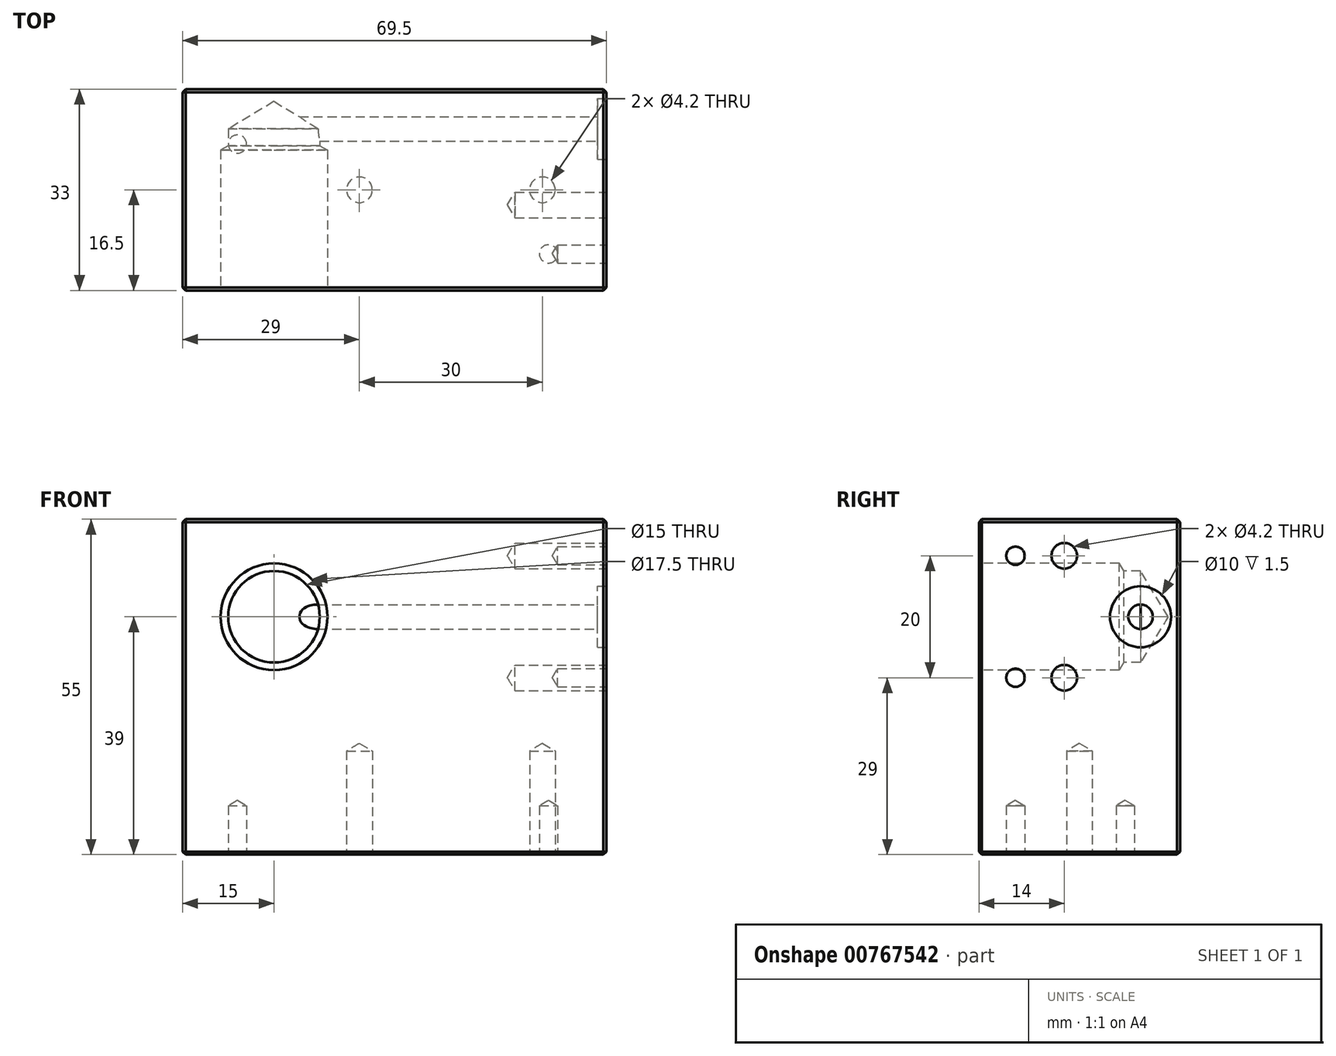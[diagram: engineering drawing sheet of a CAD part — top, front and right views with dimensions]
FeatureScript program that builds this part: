
annotation { "Feature Type Name" : "Feature", "Feature Type Description" : "" }
export const myFeature = defineFeature(function(context is Context, id is Id, definition is map)
    precondition{}
    {
        {
            var Q0;
            Q0=qCreatedBy(makeId("Front.planeOp"),FACE);
            var sketch = newSketch(context, id + "F0", { "sketchPlane" : qUnion([Q0])});
            skLineSegment(sketch, "E0.bottom", {"start": v(0, 0) * mm, "end": v(69.5, 0) * mm});
            skLineSegment(sketch, "E0.top", {"start": v(0, 55) * mm, "end": v(69.5, 55) * mm});
            skLineSegment(sketch, "E0.left", {"start": v(0, 0) * mm, "end": v(0, 55) * mm});
            skLineSegment(sketch, "E0.right", {"start": v(69.5, 0) * mm, "end": v(69.5, 55) * mm});
            skSolve(sketch);
        }
        {
            var Q0;
            Q0 = qSketchRegion(id + "F0", true);
            extrude(context, id + "F1", {"entities" : qUnion([Q0]), "oppositeDirection" : true, "depth" : 33 * mm, "offsetDistance" : 25 * mm});
        }
        {
            var Q0;
            Q0=makeQuery(id+"F1.opExtrude","CAP_FACE",FACE,{"disambiguationData":[OSD([sQuery(id+"F0.wireOp",EDGE,"E0.bottom"),sQuery(id+"F0.wireOp",EDGE,"E0.top"),sQuery(id+"F0.wireOp",EDGE,"E0.left"),sQuery(id+"F0.wireOp",EDGE,"E0.right")])],"isStart":true});
            var Q1;
            Q1=makeQuery(id+"F1.opExtrude","CAP_FACE",FACE,{"disambiguationData":[OSD([sQuery(id+"F0.wireOp",EDGE,"E0.bottom"),sQuery(id+"F0.wireOp",EDGE,"E0.top"),sQuery(id+"F0.wireOp",EDGE,"E0.left"),sQuery(id+"F0.wireOp",EDGE,"E0.right")])],"isStart":false});
            var Q2;
            Q2=makeQuery(id+"F1.opExtrude","SWEPT_FACE",FACE,{"disambiguationData":[OSD([sQuery(id+"F0.wireOp",EDGE,"E0.top")])]});
            var Q3;
            Q3=makeQuery(id+"F1.opExtrude","SWEPT_FACE",FACE,{"disambiguationData":[OSD([sQuery(id+"F0.wireOp",EDGE,"E0.left")])]});
            var Q4;
            Q4=makeQuery(id+"F1.opExtrude","SWEPT_FACE",FACE,{"disambiguationData":[OSD([sQuery(id+"F0.wireOp",EDGE,"E0.right")])]});
            var Q5;
            Q5=makeQuery(id+"F1.opExtrude","SWEPT_FACE",FACE,{"disambiguationData":[OSD([sQuery(id+"F0.wireOp",EDGE,"E0.bottom")])]});
            chamfer(context, id + "F2", {"entities" : qUnion([Q0, Q1, Q2, Q3, Q4, Q5]), "width" : 0.5 * mm, "tangentPropagation" : true});
        }
        {
            var Q0;
            Q0=qCreatedBy(makeId("Front.planeOp"),FACE);
            var sketch = newSketch(context, id + "F3", { "sketchPlane" : qUnion([Q0])});
            skPoint(sketch, "E1", {"position": v(15, 39) * mm});
            skSolve(sketch);
        }
        {
            var Q0;
            Q0=sQuery(id+"F3.wireOp",VERTEX,"E1");
            var Q1;
            Q1=makeQuery(id+"F1.opExtrude","SWEPT_BODY",BODY,{"disambiguationData":[OSD([sQuery(id+"F0.wireOp",EDGE,"E0.bottom"),sQuery(id+"F0.wireOp",EDGE,"E0.top"),sQuery(id+"F0.wireOp",EDGE,"E0.left"),sQuery(id+"F0.wireOp",EDGE,"E0.right")])]});
            hole(context, id + "F4", {"style" : HoleStyle.SIMPLE, "endStyle" : HoleEndStyle.BLIND, "standardTappedOrClearance" : lookupTablePath({ "standard" : "ISO", "engagement" : "75%", "pitch" : "2.5 mm", "size" : "M20", "type" : "Tapped" }), "standardBlindInLast" : lookupTablePath({ "standard" : "ISO", "engagement" : "75%", "pitch" : "2.5 mm", "size" : "M20", "type" : "Tapped" }), "holeDiameter" : 17.5 * mm, "majorDiameter" : 20 * mm, "showTappedDepth" : true, "holeDepth" : 23 * mm, "tappedDepth" : 18 * mm, "tapClearance" : 2, "startFromSketch" : true, "locations" : qUnion([Q0]), "scope" : qUnion([Q1])});
        }
        {
            var Q0;
            Q0=sQuery(id+"F3.wireOp",VERTEX,"E1");
            var Q1;
            Q1=makeQuery(id+"F1.opExtrude","SWEPT_BODY",BODY,{"disambiguationData":[OSD([sQuery(id+"F0.wireOp",EDGE,"E0.bottom"),sQuery(id+"F0.wireOp",EDGE,"E0.top"),sQuery(id+"F0.wireOp",EDGE,"E0.left"),sQuery(id+"F0.wireOp",EDGE,"E0.right")])]});
            hole(context, id + "F5", {"style" : HoleStyle.SIMPLE, "endStyle" : HoleEndStyle.BLIND, "holeDiameter" : 15 * mm, "majorDiameter" : 20 * mm, "holeDepth" : 26.5 * mm, "tappedDepth" : 18 * mm, "tapClearance" : 2, "startFromSketch" : true, "locations" : qUnion([Q0]), "scope" : qUnion([Q1])});
        }
        {
            var Q0;
            Q0=makeQuery(id+"F1.opExtrude","SWEPT_FACE",FACE,{"disambiguationData":[OSD([sQuery(id+"F0.wireOp",EDGE,"E0.right")])]});
            var sketch = newSketch(context, id + "F6", { "sketchPlane" : qUnion([Q0])});
            skPoint(sketch, "E2", {"position": v(26.5, 39) * mm});
            skPoint(sketch, "E3", {"position": v(14, 49) * mm});
            skPoint(sketch, "E4", {"position": v(14, 29) * mm});
            skPoint(sketch, "E5", {"position": v(6, 49) * mm});
            skPoint(sketch, "E6", {"position": v(6, 29) * mm});
            skLineSegment(sketch, "E7", {"start": v(6, 49) * mm, "end": v(6, 29) * mm, "construction": true});
            skLineSegment(sketch, "E8", {"start": v(14, 49) * mm, "end": v(14, 29) * mm, "construction": true});
            skLineSegment(sketch, "E9", {"start": v(6, 49) * mm, "end": v(14, 49) * mm, "construction": true});
            skLineSegment(sketch, "E10", {"start": v(6, 29) * mm, "end": v(14, 29) * mm, "construction": true});
            skSolve(sketch);
        }
        {
            var Q0;
            Q0=qCreatedBy(makeId("Top.planeOp"),FACE);
            var sketch = newSketch(context, id + "F7", { "sketchPlane" : qUnion([Q0])});
            skPoint(sketch, "E11", {"position": v(9, 24) * mm});
            skPoint(sketch, "E12", {"position": v(60, 6) * mm});
            skPoint(sketch, "E13", {"position": v(59, 16.5) * mm});
            skPoint(sketch, "E14", {"position": v(29, 16.5) * mm});
            skLineSegment(sketch, "E15", {"start": v(29, 16.5) * mm, "end": v(59, 16.5) * mm, "construction": true});
            skSolve(sketch);
        }
        {
            var Q0;
            Q0=sQuery(id+"F6.wireOp",VERTEX,"E2");
            var Q1;
            Q1=makeQuery(id+"F1.opExtrude","SWEPT_BODY",BODY,{"disambiguationData":[OSD([sQuery(id+"F0.wireOp",EDGE,"E0.bottom"),sQuery(id+"F0.wireOp",EDGE,"E0.top"),sQuery(id+"F0.wireOp",EDGE,"E0.left"),sQuery(id+"F0.wireOp",EDGE,"E0.right")])]});
            hole(context, id + "F8", {"style" : HoleStyle.C_BORE, "endStyle" : HoleEndStyle.BLIND, "holeDiameter" : 4 * mm, "cBoreDiameter" : 10 * mm, "cBoreDepth" : 1.5 * mm, "majorDiameter" : 5 * mm, "holeDepth" : (69.5 - 15) * mm, "tappedDepth" : 18 * mm, "tapClearance" : 2, "startFromSketch" : true, "locations" : qUnion([Q0]), "scope" : qUnion([Q1])});
        }
        {
            var Q0;
            Q0=sQuery(id+"F6.wireOp",VERTEX,"E3");
            var Q1;
            Q1=sQuery(id+"F6.wireOp",VERTEX,"E4");
            var Q2;
            Q2=makeQuery(id+"F1.opExtrude","SWEPT_BODY",BODY,{"disambiguationData":[OSD([sQuery(id+"F0.wireOp",EDGE,"E0.bottom"),sQuery(id+"F0.wireOp",EDGE,"E0.top"),sQuery(id+"F0.wireOp",EDGE,"E0.left"),sQuery(id+"F0.wireOp",EDGE,"E0.right")])]});
            hole(context, id + "F9", {"style" : HoleStyle.SIMPLE, "endStyle" : HoleEndStyle.BLIND, "standardTappedOrClearance" : lookupTablePath({ "standard" : "ISO", "engagement" : "75%", "pitch" : "0.8 mm", "size" : "M5", "type" : "Tapped" }), "standardBlindInLast" : lookupTablePath({ "standard" : "ISO", "engagement" : "75%", "pitch" : "0.8 mm", "size" : "M5", "type" : "Tapped" }), "holeDiameter" : 4.2 * mm, "majorDiameter" : 5 * mm, "showTappedDepth" : true, "holeDepth" : 15 * mm, "tappedDepth" : 11.8 * mm, "tapClearance" : 4, "startFromSketch" : true, "locations" : qUnion([Q0, Q1]), "scope" : qUnion([Q2])});
        }
        {
            var Q0;
            Q0=sQuery(id+"F6.wireOp",VERTEX,"E5");
            var Q1;
            Q1=sQuery(id+"F6.wireOp",VERTEX,"E6");
            var Q2;
            Q2=makeQuery(id+"F1.opExtrude","SWEPT_BODY",BODY,{"disambiguationData":[OSD([sQuery(id+"F0.wireOp",EDGE,"E0.bottom"),sQuery(id+"F0.wireOp",EDGE,"E0.top"),sQuery(id+"F0.wireOp",EDGE,"E0.left"),sQuery(id+"F0.wireOp",EDGE,"E0.right")])]});
            hole(context, id + "F10", {"style" : HoleStyle.SIMPLE, "endStyle" : HoleEndStyle.BLIND, "holeDiameter" : 3 * mm, "majorDiameter" : 5 * mm, "holeDepth" : 8 * mm, "tappedDepth" : 11.8 * mm, "tapClearance" : 4, "startFromSketch" : true, "locations" : qUnion([Q0, Q1]), "scope" : qUnion([Q2])});
        }
        {
            var Q0;
            Q0=sQuery(id+"F7.wireOp",VERTEX,"E11");
            var Q1;
            Q1=sQuery(id+"F7.wireOp",VERTEX,"E12");
            var Q2;
            Q2=makeQuery(id+"F1.opExtrude","SWEPT_BODY",BODY,{"disambiguationData":[OSD([sQuery(id+"F0.wireOp",EDGE,"E0.bottom"),sQuery(id+"F0.wireOp",EDGE,"E0.top"),sQuery(id+"F0.wireOp",EDGE,"E0.left"),sQuery(id+"F0.wireOp",EDGE,"E0.right")])]});
            hole(context, id + "F11", {"style" : HoleStyle.SIMPLE, "endStyle" : HoleEndStyle.BLIND, "oppositeDirection" : true, "holeDiameter" : 3 * mm, "majorDiameter" : 5 * mm, "holeDepth" : 8 * mm, "tappedDepth" : 11.8 * mm, "tapClearance" : 4, "startFromSketch" : true, "locations" : qUnion([Q0, Q1]), "scope" : qUnion([Q2])});
        }
        {
            var Q0;
            Q0=sQuery(id+"F7.wireOp",VERTEX,"E14");
            var Q1;
            Q1=sQuery(id+"F7.wireOp",VERTEX,"E13");
            var Q2;
            Q2=makeQuery(id+"F1.opExtrude","SWEPT_BODY",BODY,{"disambiguationData":[OSD([sQuery(id+"F0.wireOp",EDGE,"E0.bottom"),sQuery(id+"F0.wireOp",EDGE,"E0.top"),sQuery(id+"F0.wireOp",EDGE,"E0.left"),sQuery(id+"F0.wireOp",EDGE,"E0.right")])]});
            hole(context, id + "F12", {"style" : HoleStyle.SIMPLE, "endStyle" : HoleEndStyle.BLIND, "oppositeDirection" : true, "standardTappedOrClearance" : lookupTablePath({ "standard" : "ISO", "engagement" : "75%", "pitch" : "0.8 mm", "size" : "M5", "type" : "Tapped" }), "standardBlindInLast" : lookupTablePath({ "standard" : "ISO", "engagement" : "75%", "pitch" : "0.8 mm", "size" : "M5", "type" : "Tapped" }), "holeDiameter" : 4.2 * mm, "majorDiameter" : 5 * mm, "showTappedDepth" : true, "holeDepth" : 17 * mm, "tappedDepth" : 13.8 * mm, "tapClearance" : 4, "startFromSketch" : true, "locations" : qUnion([Q0, Q1]), "scope" : qUnion([Q2])});
        }
    });
